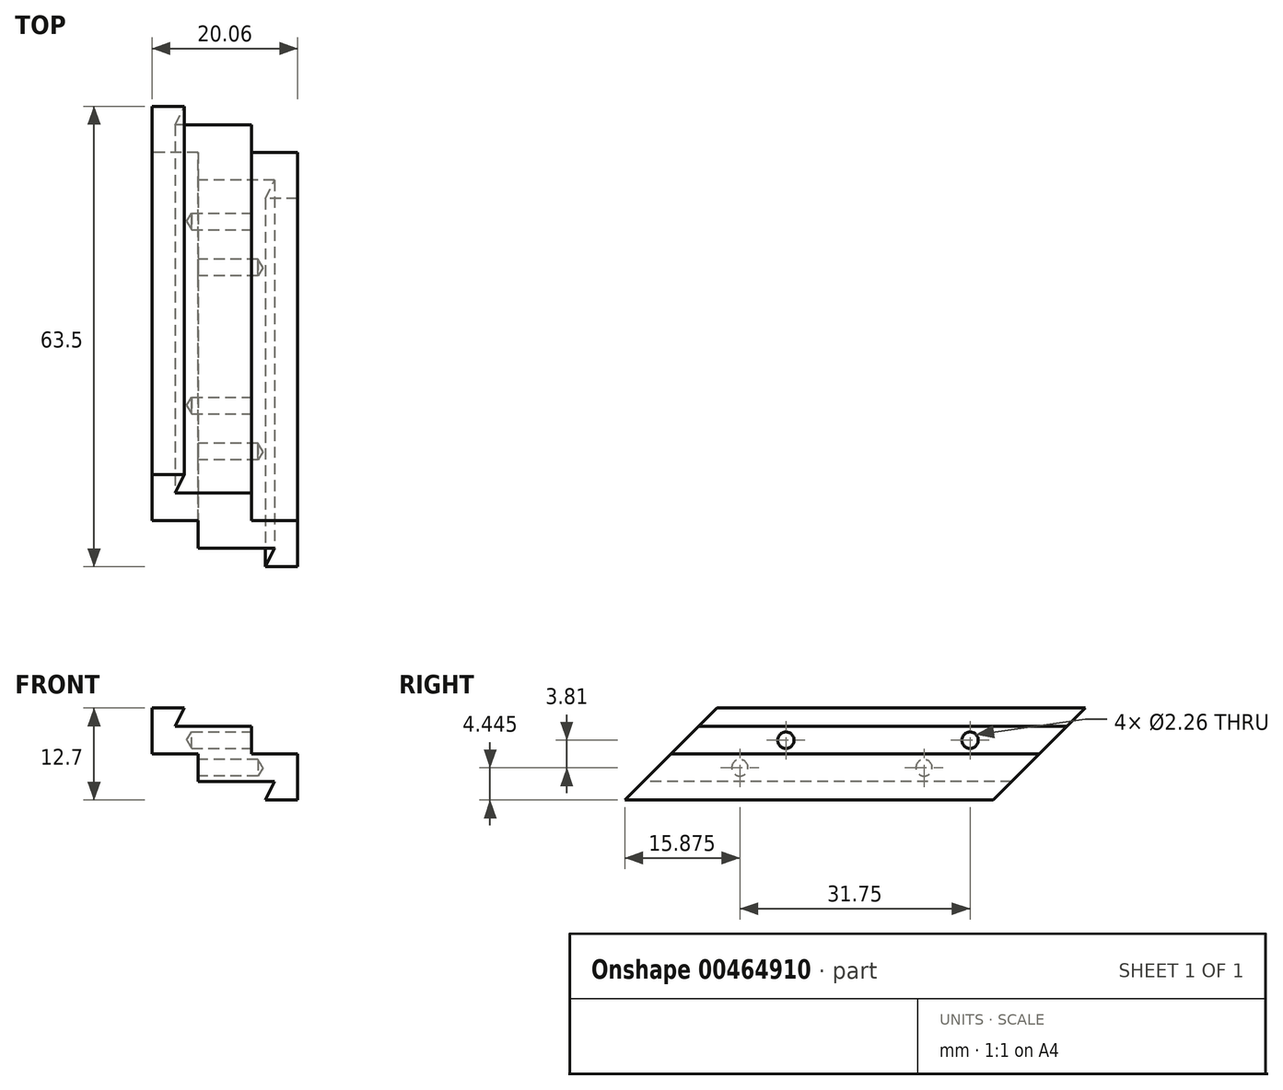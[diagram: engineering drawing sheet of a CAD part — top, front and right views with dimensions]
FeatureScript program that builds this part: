
annotation { "Feature Type Name" : "Feature", "Feature Type Description" : "" }
export const myFeature = defineFeature(function(context is Context, id is Id, definition is map)
    precondition{}
    {
        {
            var Q0;
            Q0=qCreatedBy(makeId("Right.planeOp"),FACE);
            var sketch = newSketch(context, id + "F0", { "sketchPlane" : qUnion([Q0])});
            skLineSegment(sketch, "E0.bottom", {"start": v(31.75, 6.35) * mm, "end": v(-19.05, 6.35) * mm});
            skLineSegment(sketch, "E0.top", {"start": v(19.05, -6.35) * mm, "end": v(-31.75, -6.35) * mm});
            skPoint(sketch, "E0.middle", {"position": v(0, 0) * mm});
            skLineSegment(sketch, "E1", {"start": v(-31.75, -6.35) * mm, "end": v(-19.05, 6.35) * mm});
            skLineSegment(sketch, "E2", {"start": v(31.75, 6.35) * mm, "end": v(19.05, -6.35) * mm});
            skSolve(sketch);
        }
        {
            var Q0;
            Q0=qSketchRegion(id+"F0",true);
            extrude(context, id + "F1", {"entities" : qUnion([Q0]), "endBound" : BoundingType.SYMMETRIC, "depth" : 20.07 * mm});
        }
        {
            var Q0;
            Q0=qCreatedBy(makeId("Front.planeOp"),FACE);
            var sketch = newSketch(context, id + "F2", { "sketchPlane" : qUnion([Q0])});
            skLineSegment(sketch, "E3", {"start": v(0, 1.15) * mm, "end": v(0, -10.33) * mm, "construction": true});
            skLineSegment(sketch, "E4", {"start": v(-5.59, -6.35) * mm, "end": v(-6.86, -3.81) * mm});
            skLineSegment(sketch, "E5", {"start": v(-6.86, -3.81) * mm, "end": v(6.86, -3.81) * mm});
            skLineSegment(sketch, "E6", {"start": v(6.86, -3.81) * mm, "end": v(5.59, -6.35) * mm});
            skLineSegment(sketch, "E7", {"start": v(5.59, -6.35) * mm, "end": v(-5.59, -6.35) * mm});
            skLineSegment(sketch, "E8", {"start": v(-14.86, 0) * mm, "end": v(21.63, 0) * mm, "construction": true});
            skLineSegment(sketch, "E9.MirrorCS", {"start": v(-5.59, 6.35) * mm, "end": v(-6.86, 3.81) * mm});
            skLineSegment(sketch, "E10.MirrorCS", {"start": v(-6.86, 3.81) * mm, "end": v(6.86, 3.81) * mm});
            skLineSegment(sketch, "E11.MirrorCS", {"start": v(5.59, 6.35) * mm, "end": v(-5.59, 6.35) * mm});
            skLineSegment(sketch, "E12.MirrorCS", {"start": v(6.86, 3.81) * mm, "end": v(5.59, 6.35) * mm});
            skSolve(sketch);
        }
        {
            var Q0;
            Q0=qSketchRegion(id+"F2",true);
            extrude(context, id + "F3", {"entities" : qUnion([Q0]), "operationType" : NewBodyOperationType.REMOVE, "endBound" : BoundingType.SYMMETRIC, "oppositeDirection" : true, "depth" : 152.4 * mm});
        }
        {
            var Q0;
            Q0=qCreatedBy(makeId("Front.planeOp"),FACE);
            var sketch = newSketch(context, id + "F4", { "sketchPlane" : qUnion([Q0])});
            skLineSegment(sketch, "E13.bottom", {"start": v(3.68, 0) * mm, "end": v(10.03, 0) * mm});
            skLineSegment(sketch, "E13.top", {"start": v(3.68, 6.35) * mm, "end": v(10.03, 6.35) * mm});
            skLineSegment(sketch, "E13.left", {"start": v(3.68, 0) * mm, "end": v(3.68, 6.35) * mm});
            skLineSegment(sketch, "E13.right", {"start": v(10.03, 0) * mm, "end": v(10.03, 6.35) * mm});
            skLineSegment(sketch, "E14.bottom", {"start": v(-3.68, 0) * mm, "end": v(-10.03, 0) * mm});
            skLineSegment(sketch, "E14.top", {"start": v(-3.68, -6.35) * mm, "end": v(-10.03, -6.35) * mm});
            skLineSegment(sketch, "E14.left", {"start": v(-3.68, 0) * mm, "end": v(-3.68, -6.35) * mm});
            skLineSegment(sketch, "E14.right", {"start": v(-10.03, 0) * mm, "end": v(-10.03, -6.35) * mm});
            skSolve(sketch);
        }
        {
            var Q0;
            Q0 = qSketchRegion(id + "F4", true);
            extrude(context, id + "F5", {"entities" : qUnion([Q0]), "operationType" : NewBodyOperationType.REMOVE, "endBound" : BoundingType.SYMMETRIC, "depth" : 152.4 * mm});
        }
        {
            var Q0;
            Q0=makeQuery(id+"F5.boolean.opBoolean","COPY",FACE,{"derivedFrom":makeQuery(id+"F5.opExtrude","SWEPT_FACE",FACE,{"disambiguationData":[OSD([sQuery(id+"F4.wireOp",EDGE,"E13.left")])]})});
            var sketch = newSketch(context, id + "F6", { "sketchPlane" : qUnion([Q0])});
            skCircle(sketch, "E15", {"center": v(-9.53, 1.9) * mm, "radius": 1.9 * mm});
            skCircle(sketch, "E16", {"center": v(15.88, 1.9) * mm, "radius": 1.9 * mm});
            skSolve(sketch);
        }
        {
            var Q0;
            Q0=sQuery(id+"F6.wireOp",VERTEX,"E15.center");
            var Q1;
            Q1=sQuery(id+"F6.wireOp",VERTEX,"E16.center");
            var Q2;
            Q2=makeQuery(id+"F1.opExtrude","SWEPT_BODY",BODY,{"disambiguationData":[OSD([sQuery(id+"F0.wireOp",EDGE,"E0.bottom"),sQuery(id+"F0.wireOp",EDGE,"E0.top"),sQuery(id+"F0.wireOp",EDGE,"E1"),sQuery(id+"F0.wireOp",EDGE,"E2")])]});
            hole(context, id + "F7", {"style" : HoleStyle.SIMPLE, "endStyle" : HoleEndStyle.BLIND, "standardTappedOrClearance" : lookupTablePath({ "standard" : "ANSI", "engagement" : "75%", "pitch" : "40 tpi", "size" : "#4", "type" : "Tapped" }), "standardBlindInLast" : lookupTablePath({ "standard" : "ANSI", "engagement" : "75%", "pitch" : "40 tpi", "size" : "#4", "type" : "Tapped" }), "holeDiameter" : 2.26 * mm, "showTappedDepth" : true, "holeDepth" : 8.26 * mm, "tappedDepth" : 6.35 * mm, "tapClearance" : 3, "locations" : qUnion([Q0, Q1]), "scope" : qUnion([Q2]), "majorDiameter" : 2.84 * mm});
        }
        {
            var Q0;
            Q0=makeQuery(id+"F5.boolean.opBoolean","COPY",FACE,{"derivedFrom":makeQuery(id+"F5.opExtrude","SWEPT_FACE",FACE,{"disambiguationData":[OSD([sQuery(id+"F4.wireOp",EDGE,"E14.left")])]})});
            var sketch = newSketch(context, id + "F8", { "sketchPlane" : qUnion([Q0])});
            skCircle(sketch, "E17", {"center": v(-9.53, -1.9) * mm, "radius": 1.9 * mm});
            skCircle(sketch, "E18", {"center": v(15.88, -1.9) * mm, "radius": 1.9 * mm});
            skSolve(sketch);
        }
        {
            var Q0;
            Q0=sQuery(id+"F8.wireOp",VERTEX,"E17.center");
            var Q1;
            Q1=sQuery(id+"F8.wireOp",VERTEX,"E18.center");
            var Q2;
            Q2=makeQuery(id+"F1.opExtrude","SWEPT_BODY",BODY,{"disambiguationData":[OSD([sQuery(id+"F0.wireOp",EDGE,"E0.bottom"),sQuery(id+"F0.wireOp",EDGE,"E0.top"),sQuery(id+"F0.wireOp",EDGE,"E1"),sQuery(id+"F0.wireOp",EDGE,"E2")])]});
            hole(context, id + "F9", {"style" : HoleStyle.SIMPLE, "endStyle" : HoleEndStyle.BLIND, "standardTappedOrClearance" : lookupTablePath({ "standard" : "ANSI", "engagement" : "75%", "pitch" : "40 tpi", "size" : "#4", "type" : "Tapped" }), "standardBlindInLast" : lookupTablePath({ "standard" : "ANSI", "engagement" : "75%", "pitch" : "40 tpi", "size" : "#4", "type" : "Tapped" }), "holeDiameter" : 2.26 * mm, "showTappedDepth" : true, "holeDepth" : 8.26 * mm, "tappedDepth" : 6.35 * mm, "tapClearance" : 3, "locations" : qUnion([Q0, Q1]), "scope" : qUnion([Q2]), "majorDiameter" : 2.84 * mm});
        }
    });
